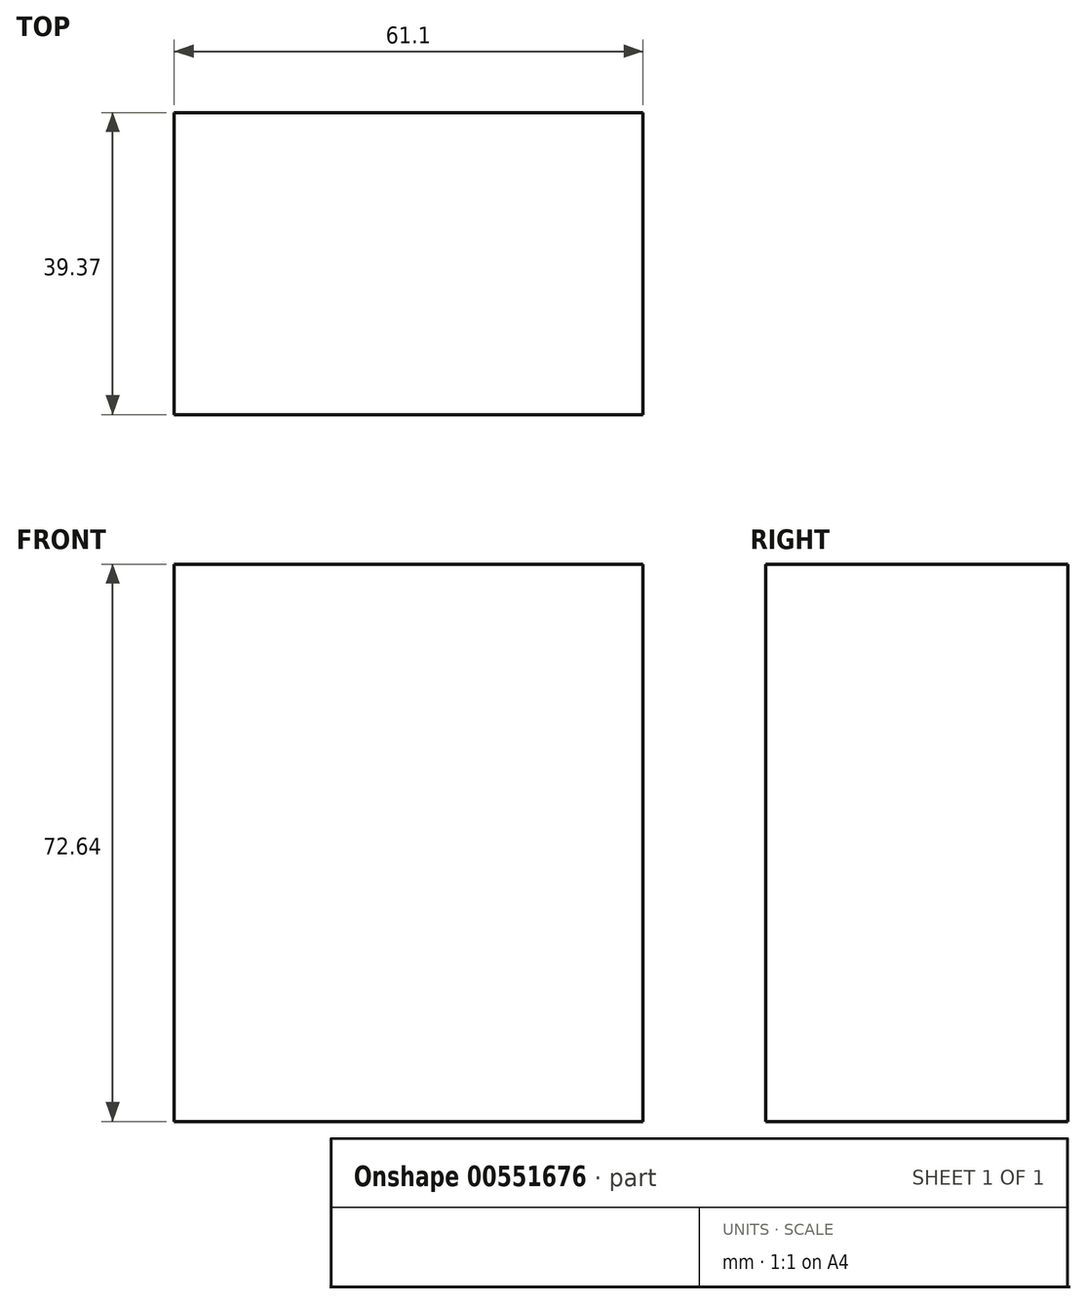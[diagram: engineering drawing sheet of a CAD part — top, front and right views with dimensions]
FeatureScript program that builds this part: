
annotation { "Feature Type Name" : "Feature", "Feature Type Description" : "" }
export const myFeature = defineFeature(function(context is Context, id is Id, definition is map)
    precondition{}
    {
        {
            var Q0;
            Q0=qCreatedBy(makeId("Front.planeOp"),FACE);
            var sketch = newSketch(context, id + "F0", { "sketchPlane" : qUnion([Q0])});
            skLineSegment(sketch, "E0.bottom", {"start": v(-30.55, 33.6) * mm, "end": v(30.55, 33.6) * mm});
            skLineSegment(sketch, "E0.top", {"start": v(-30.55, -39.04) * mm, "end": v(30.55, -39.04) * mm});
            skLineSegment(sketch, "E0.left", {"start": v(-30.55, 33.6) * mm, "end": v(-30.55, -39.04) * mm});
            skLineSegment(sketch, "E0.right", {"start": v(30.55, 33.6) * mm, "end": v(30.55, -39.04) * mm});
            skSolve(sketch);
        }
        {
            var Q0;
            Q0 = qSketchRegion(id + "F0", true);
            extrude(context, id + "F1", {"entities" : qUnion([Q0]), "depth" : 39.37 * mm, "offsetDistance" : 25.4 * mm});
        }
    });
